# Revit family: TL 2D_Tracklok_Vert_SPT-10V
name_source: partatom
category: Detail Items
revit_build: Autodesk Revit 2016 (Build: 20150714_1515(x64)
units: mm (PartAtom-declared; Revit-internal decimal feet)

## family parameters
Rotate with component = No
Shared = No

## types (13) — shared parameters

## per-type parameters (varying)
| type | Gaplok End | Gaplok Plan | Gaplok Side | Tracklok Retro-Elev | Tracklok Retro-Plan | Tracklok Timba-Elev | Tracklok Timba-Plan | Tracklok Vert-End Elev | Tracklok Vert-Plan | Tracklok Vert-Side Elev |
| Vert-Plan | No | No | No | No | No | No | No | No | Yes | No |
| Vert-Side | No | No | No | No | No | No | No | No | No | Yes |
| Vert-End | No | No | No | No | No | No | No | Yes | No | No |
| Bracket to level above | No | No | No | No | No | No | No | No | No | No |
| Vert_Retro-Side | No | No | No | Yes | No | No | No | No | No | Yes |
| Vert_Retro-End | No | No | No | Yes | No | No | No | Yes | No | No |
| Vert_Timba-Plan | No | No | No | No | No | No | Yes | No | Yes | No |
| Vert_Timba-End | No | No | No | No | No | Yes | No | Yes | No | No |
| Vert_Timba-Side | No | No | No | No | No | Yes | No | No | No | Yes |
| Vert_Retro-Plan | No | No | No | No | Yes | No | No | No | Yes | No |
| Vert_Gaplok-Plan | No | Yes | No | No | No | No | No | No | Yes | No |
| Vert_Gaplok-End | No | No | Yes | No | No | No | No | Yes | No | No |
| Vert_Gaplok-Side | Yes | No | No | No | No | No | No | No | No | Yes |

type visibility flags (boolean, named after types; folded from table):
- Vert-Plan: Yes: (none)
- Vert-Side: Yes: (none)
- Vert-End: Yes: (none)
- Bracket to level above: Yes: Bracket to level above
- Vert_Retro-Side: Yes: (none)
- Vert_Retro-End: Yes: (none)
- Vert_Timba-Plan: Yes: (none)
- Vert_Timba-End: Yes: (none)
- Vert_Timba-Side: Yes: (none)
- Vert_Retro-Plan: Yes: (none)
- Vert_Gaplok-Plan: Yes: (none)
- Vert_Gaplok-End: Yes: (none)
- Vert_Gaplok-Side: Yes: (none)

## geometry (parser evidence)
native form markers: Sweep x1
no freeform markers — native parametric forms only
